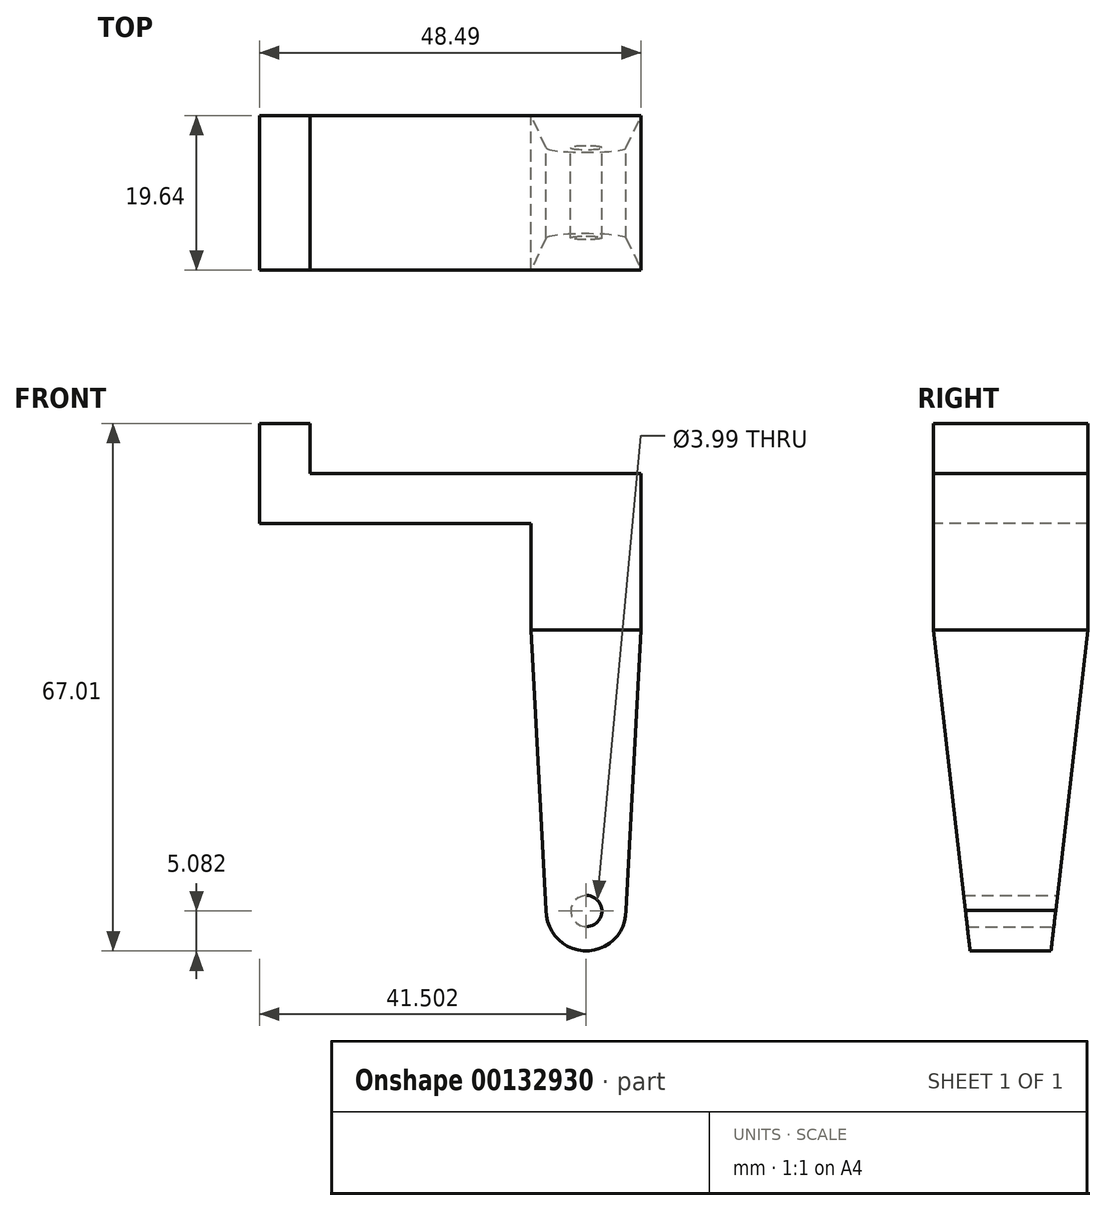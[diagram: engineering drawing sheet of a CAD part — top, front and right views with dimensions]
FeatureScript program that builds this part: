
annotation { "Feature Type Name" : "Feature", "Feature Type Description" : "" }
export const myFeature = defineFeature(function(context is Context, id is Id, definition is map)
    precondition{}
    {
        {
            var Q0;
            Q0=qCreatedBy(makeId("Top.planeOp"),FACE);
            var sketch = newSketch(context, id + "F0", { "sketchPlane" : qUnion([Q0])});
            skLineSegment(sketch, "E0.bottom", {"start": v(-25.76, 27.5) * mm, "end": v(22.73, 27.5) * mm});
            skLineSegment(sketch, "E0.top", {"start": v(-25.76, 7.87) * mm, "end": v(22.73, 7.87) * mm});
            skLineSegment(sketch, "E0.left", {"start": v(-25.76, 27.5) * mm, "end": v(-25.76, 7.87) * mm});
            skLineSegment(sketch, "E0.right", {"start": v(22.73, 27.5) * mm, "end": v(22.73, 7.87) * mm});
            skLineSegment(sketch, "E1", {"start": v(-19.31, 27.5) * mm, "end": v(-19.31, 7.87) * mm});
            skPoint(sketch, "E1.endSnap0", {"position": v(-1.52, 7.87) * mm});
            skLineSegment(sketch, "E2", {"start": v(8.76, 27.5) * mm, "end": v(8.76, 7.87) * mm});
            skSolve(sketch);
        }
        {
            var Q0;
            {var subQ0=sQuery(id+"F0.wireOp",EDGE,"E0.left");Q0=makeQuery(id+"F0.imprint","IMPRINT",FACE,{"disambiguationData":[TD([[makeQuery(id+"F0.imprint","IMPRINT",EDGE,{"derivedFrom":subQ0}),1.0]])]});}
            var Q1;
            {var subQ0=sQuery(id+"F0.wireOp",EDGE,"E1");Q1=makeQuery(id+"F0.imprint","IMPRINT",FACE,{"disambiguationData":[TD([[makeQuery(id+"F0.imprint","IMPRINT",EDGE,{"derivedFrom":subQ0}),1.0]])]});}
            var Q2;
            {var subQ0=sQuery(id+"F0.wireOp",EDGE,"E0.right");Q2=makeQuery(id+"F0.imprint","IMPRINT",FACE,{"disambiguationData":[TD([[makeQuery(id+"F0.imprint","IMPRINT",EDGE,{"derivedFrom":subQ0}),-1.0]])]});}
            extrude(context, id + "F1", {"entities" : qUnion([Q0, Q1, Q2]), "oppositeDirection" : true, "depth" : 6.35 * mm});
        }
        {
            var Q0;
            {var subQ0=sQuery(id+"F0.wireOp",EDGE,"E0.left");Q0=makeQuery(id+"F0.imprint","IMPRINT",FACE,{"disambiguationData":[TD([[makeQuery(id+"F0.imprint","IMPRINT",EDGE,{"derivedFrom":subQ0}),1.0]])]});}
            extrude(context, id + "F2", {"entities" : qUnion([Q0]), "operationType" : NewBodyOperationType.ADD, "depth" : 6.35 * mm});
        }
        {
            var Q0;
            {var subQ0=sQuery(id+"F0.wireOp",EDGE,"E0.right");Q0=makeQuery(id+"F0.imprint","IMPRINT",FACE,{"disambiguationData":[TD([[makeQuery(id+"F0.imprint","IMPRINT",EDGE,{"derivedFrom":subQ0}),-1.0]])]});}
            extrude(context, id + "F3", {"entities" : qUnion([Q0]), "operationType" : NewBodyOperationType.ADD, "oppositeDirection" : true, "depth" : 60.96 * mm});
        }
        {
            var Q0;
            {var subQ0=sQuery(id+"F0.wireOp",EDGE,"E0.bottom");Q0=makeQuery(id+"F3.boolean.opBoolean","MERGE",FACE,{"derivedFrom":[makeQuery(id+"F2.boolean.opBoolean","MERGE",FACE,{"derivedFrom":[makeQuery(id+"F1.opExtrude","SWEPT_FACE",FACE,{"disambiguationData":[OSD([subQ0])]}),makeQuery(id+"F2.opExtrude","SWEPT_FACE",FACE,{"disambiguationData":[OSD([subQ0])]})]}),makeQuery(id+"F3.opExtrude","SWEPT_FACE",FACE,{"disambiguationData":[OSD([subQ0])]})]});}
            var sketch = newSketch(context, id + "F4", { "sketchPlane" : qUnion([Q0])});
            skCircle(sketch, "E3", {"center": v(-15.74, -55.58) * mm, "radius": 2 * mm});
            skPoint(sketch, "E3.centerSnap0", {"position": v(-15.74, -60.96) * mm});
            skCircle(sketch, "E4", {"center": v(-15.74, -55.58) * mm, "radius": 5.08 * mm});
            skLineSegment(sketch, "E5", {"start": v(-10.66, -55.48) * mm, "end": v(-8.76, -19.88) * mm});
            skLineSegment(sketch, "E6", {"start": v(-15.74, -55.58) * mm, "end": v(-15.74, -19.88) * mm, "construction": true});
            skLineSegment(sketch, "E7.MirrorCS", {"start": v(-20.82, -55.48) * mm, "end": v(-22.73, -19.88) * mm});
            skSolve(sketch);
        }
        {
            var Q0;
            {var subQ2=sQuery(id+"F4.wireOp",EDGE,"E5");Q0=makeQuery(id+"F4.imprint","IMPRINT",FACE,{"disambiguationData":[TD([[makeQuery(id+"F4.imprint","IMPRINT",EDGE,{"derivedFrom":subQ2}),-1.0]])]});}
            extrude(context, id + "F5", {"entities" : qUnion([Q0]), "operationType" : NewBodyOperationType.REMOVE, "endBound" : BoundingType.THROUGH_ALL, "oppositeDirection" : true, "depth" : 40.1 * mm});
        }
        {
            var Q0;
            Q0=makeQuery(id+"F4.imprint","IMPRINT",FACE,{"disambiguationData":[TD([[makeQuery(id+"F4.imprint","IMPRINT",EDGE,{"derivedFrom":sQuery(id+"F4.wireOp",EDGE,"E3")}),1.0]])]});
            extrude(context, id + "F6", {"entities" : qUnion([Q0]), "operationType" : NewBodyOperationType.REMOVE, "endBound" : BoundingType.THROUGH_ALL, "oppositeDirection" : true, "depth" : 28.1 * mm});
        }
        {
            var Q0;
            {var subQ0=sQuery(id+"F0.wireOp",EDGE,"E0.right");Q0=makeQuery(id+"F3.boolean.opBoolean","MERGE",FACE,{"derivedFrom":[makeQuery(id+"F1.opExtrude","SWEPT_FACE",FACE,{"disambiguationData":[OSD([subQ0])]}),makeQuery(id+"F3.opExtrude","SWEPT_FACE",FACE,{"disambiguationData":[OSD([subQ0])]})]});}
            var sketch = newSketch(context, id + "F7", { "sketchPlane" : qUnion([Q0])});
            skLineSegment(sketch, "E8", {"start": v(27.5, -60.66) * mm, "end": v(7.87, -60.66) * mm});
            skLineSegment(sketch, "E9", {"start": v(17.69, -69.43) * mm, "end": v(17.69, 14.35) * mm, "construction": true});
            skPoint(sketch, "E9.startSnap0", {"position": v(17.69, -60.66) * mm});
            skLineSegment(sketch, "E10", {"start": v(7.87, -19.88) * mm, "end": v(12.55, -60.66) * mm});
            skLineSegment(sketch, "E11.MirrorCS", {"start": v(27.5, -19.88) * mm, "end": v(22.83, -60.66) * mm});
            skLineSegment(sketch, "E12.0", {"start": v(27.5, -55.48) * mm, "end": v(27.5, -19.88) * mm});
            skLineSegment(sketch, "E13.0", {"start": v(27.5, -55.48) * mm, "end": v(27.5, -60.66) * mm});
            skLineSegment(sketch, "E14.0", {"start": v(7.87, -19.88) * mm, "end": v(7.87, -55.48) * mm});
            skLineSegment(sketch, "E15.0", {"start": v(7.87, -55.48) * mm, "end": v(7.87, -60.66) * mm});
            skSolve(sketch);
        }
        {
            var Q0;
            {var subQ2=sQuery(id+"F7.wireOp",EDGE,"E11.MirrorCS");Q0=makeQuery(id+"F7.imprint","IMPRINT",FACE,{"disambiguationData":[TD([[makeQuery(id+"F7.imprint","IMPRINT",EDGE,{"derivedFrom":subQ2}),1.0]])]});}
            var Q1;
            {var subQ2=sQuery(id+"F7.wireOp",EDGE,"E10");Q1=makeQuery(id+"F7.imprint","IMPRINT",FACE,{"disambiguationData":[TD([[makeQuery(id+"F7.imprint","IMPRINT",EDGE,{"derivedFrom":subQ2}),-1.0]])]});}
            extrude(context, id + "F8", {"entities" : qUnion([Q0, Q1]), "operationType" : NewBodyOperationType.REMOVE, "endBound" : BoundingType.THROUGH_ALL, "oppositeDirection" : true, "depth" : 28.64 * mm});
        }
    });
